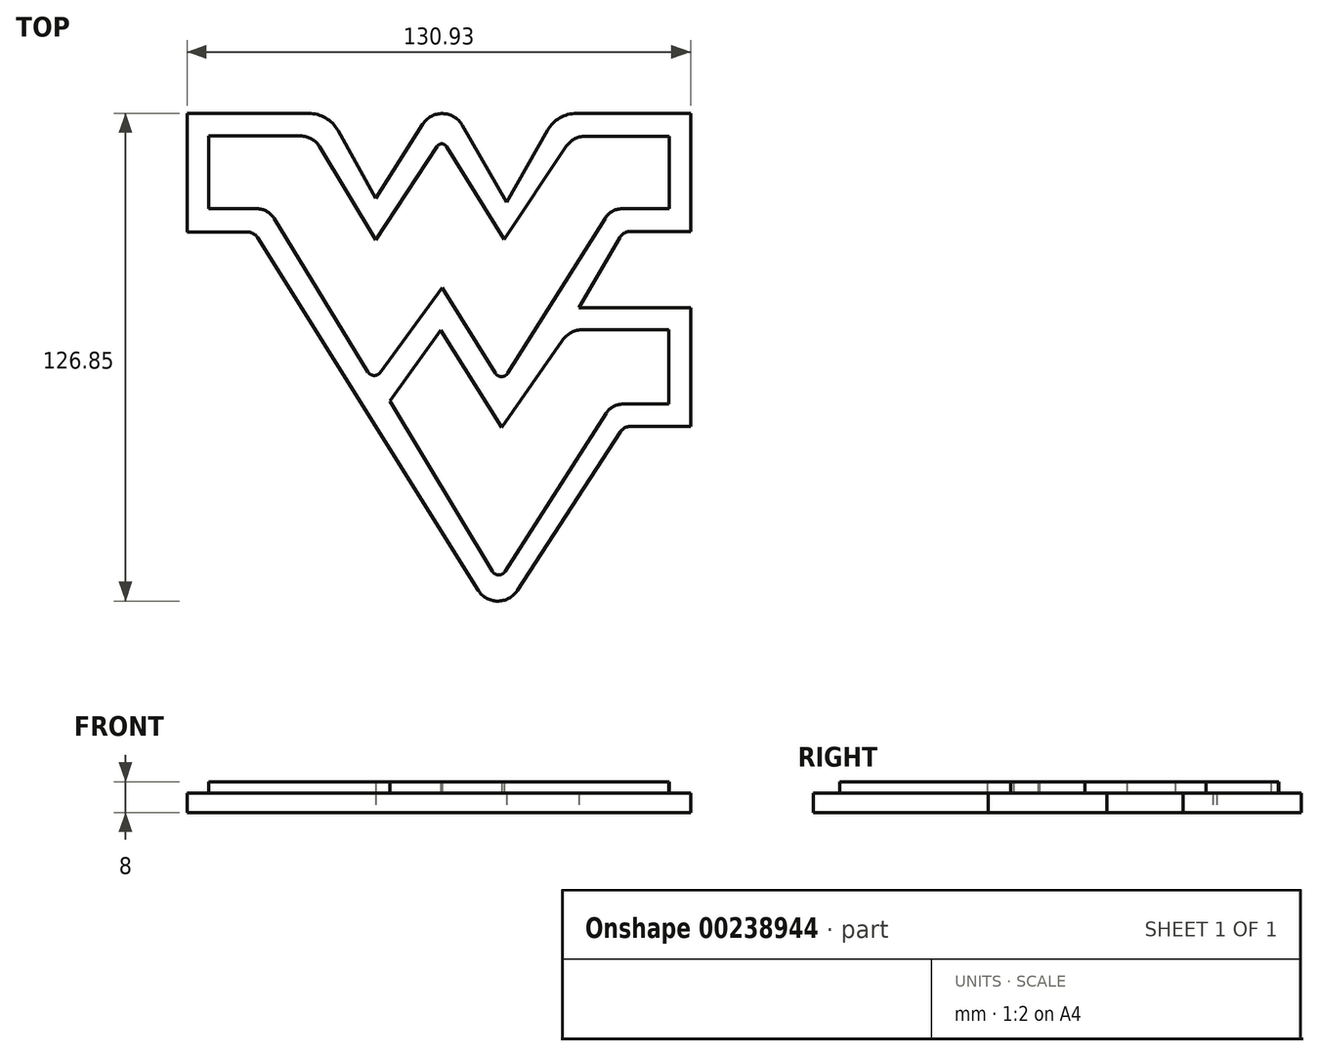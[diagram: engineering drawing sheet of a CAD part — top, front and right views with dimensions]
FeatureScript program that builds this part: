
annotation { "Feature Type Name" : "Feature", "Feature Type Description" : "" }
export const myFeature = defineFeature(function(context is Context, id is Id, definition is map)
    precondition{}
    {
        {
            var Q0;
            Q0=qCreatedBy(makeId("Top.planeOp"),FACE);
            var sketch = newSketch(context, id + "F0", { "sketchPlane" : qUnion([Q0])});
            skLineSegment(sketch, "E0", {"start": v(0, 0) * mm, "end": v(0, 127) * mm, "construction": true});
            skLineSegment(sketch, "E1", {"start": v(130.93, 127) * mm, "end": v(130.93, 96.28) * mm});
            skLineSegment(sketch, "E2", {"start": v(130.93, 45.55) * mm, "end": v(115.18, 45.55) * mm});
            skLineSegment(sketch, "E3", {"start": v(130.93, 76.4) * mm, "end": v(101.93, 76.4) * mm});
            skLineSegment(sketch, "E4", {"start": v(101.93, 76.4) * mm, "end": v(112.57, 94.78) * mm});
            skLineSegment(sketch, "E5", {"start": v(130.93, 96.28) * mm, "end": v(115.16, 96.28) * mm});
            skLineSegment(sketch, "E6", {"start": v(83.05, 103.92) * mm, "end": v(93.75, 122.62) * mm});
            skLineSegment(sketch, "E7", {"start": v(83.05, 103.92) * mm, "end": v(71.55, 123.94) * mm});
            skLineSegment(sketch, "E8", {"start": v(49.03, 104.93) * mm, "end": v(61.29, 124.17) * mm});
            skLineSegment(sketch, "E9", {"start": v(49.03, 104.93) * mm, "end": v(39.23, 122.53) * mm});
            skLineSegment(sketch, "E10", {"start": v(0, 96.14) * mm, "end": v(15.76, 96.14) * mm});
            skLineSegment(sketch, "E11", {"start": v(85.84, 2.88) * mm, "end": v(112.66, 44.18) * mm});
            skLineSegment(sketch, "E12", {"start": v(75.72, 2.96) * mm, "end": v(18.3, 94.73) * mm});
            skLineSegment(sketch, "E13.trimOffspring", {"start": v(63.09, 127) * mm, "end": v(69.8, 127) * mm});
            skLineSegment(sketch, "E14.trimOffspring", {"start": v(101.3, 127) * mm, "end": v(130.93, 127) * mm});
            skLineSegment(sketch, "E15", {"start": v(0, 127) * mm, "end": v(31.63, 127) * mm});
            skPoint(sketch, "E16.visualSharp", {"position": v(36.74, 127) * mm});
            skArc(sketch, "E16.filletArc", {"start": v(39.23, 122.53) * mm, "mid": v(36.04, 125.8) * mm, "end": v(31.63, 127) * mm});
            skPoint(sketch, "E17.visualSharp", {"position": v(96.25, 127) * mm});
            skArc(sketch, "E17.filletArc", {"start": v(101.3, 127) * mm, "mid": v(96.93, 125.83) * mm, "end": v(93.75, 122.62) * mm});
            skPoint(sketch, "E18.visualSharp", {"position": v(66.61, 132.54) * mm});
            skArc(sketch, "E18.filletArc", {"start": v(71.55, 123.94) * mm, "mid": v(66.49, 126.95) * mm, "end": v(61.29, 124.17) * mm});
            skLineSegment(sketch, "E19", {"start": v(80.71, -5.02) * mm, "end": v(0, -5.02) * mm, "construction": true});
            skLineSegment(sketch, "E20", {"start": v(0, -5.02) * mm, "end": v(0, 0) * mm, "construction": true});
            skPoint(sketch, "E21.visualSharp", {"position": v(80.71, -5.02) * mm});
            skArc(sketch, "E21.filletArc", {"start": v(75.72, 2.96) * mm, "mid": v(80.76, 0.15) * mm, "end": v(85.84, 2.88) * mm});
            skLineSegment(sketch, "E22.trimOffspring", {"start": v(130.93, 76.4) * mm, "end": v(130.93, 45.55) * mm});
            skPoint(sketch, "E23.visualSharp", {"position": v(17.42, 96.14) * mm});
            skArc(sketch, "E23.filletArc", {"start": v(18.3, 94.73) * mm, "mid": v(17.21, 95.76) * mm, "end": v(15.76, 96.14) * mm});
            skPoint(sketch, "E24.visualSharp", {"position": v(113.55, 45.55) * mm});
            skArc(sketch, "E24.filletArc", {"start": v(115.18, 45.55) * mm, "mid": v(113.75, 45.18) * mm, "end": v(112.66, 44.18) * mm});
            skPoint(sketch, "E25.visualSharp", {"position": v(113.43, 96.28) * mm});
            skArc(sketch, "E25.filletArc", {"start": v(115.16, 96.28) * mm, "mid": v(113.67, 95.88) * mm, "end": v(112.57, 94.78) * mm});
            skLineSegment(sketch, "E26", {"start": v(5.58, 121.12) * mm, "end": v(0, 121.12) * mm, "construction": true});
            skLineSegment(sketch, "E27", {"start": v(5.58, 121.12) * mm, "end": v(29.52, 121.12) * mm});
            skLineSegment(sketch, "E28", {"start": v(49.07, 94.16) * mm, "end": v(34.49, 118.31) * mm});
            skLineSegment(sketch, "E29", {"start": v(49.07, 94.16) * mm, "end": v(65.1, 118.45) * mm});
            skLineSegment(sketch, "E30", {"start": v(82.45, 94.25) * mm, "end": v(67.45, 118.42) * mm});
            skLineSegment(sketch, "E31", {"start": v(82.45, 94.25) * mm, "end": v(98.64, 118.46) * mm});
            skLineSegment(sketch, "E32", {"start": v(125.34, 121.03) * mm, "end": v(103.46, 121.03) * mm});
            skLineSegment(sketch, "E33", {"start": v(125.34, 102.18) * mm, "end": v(113.1, 102.18) * mm});
            skLineSegment(sketch, "E34", {"start": v(5.58, 121.12) * mm, "end": v(5.58, 102.18) * mm});
            skLineSegment(sketch, "E35", {"start": v(5.58, 102.18) * mm, "end": v(18.22, 102.18) * mm});
            skLineSegment(sketch, "E36", {"start": v(48.58, 57.31) * mm, "end": v(0, 57.31) * mm, "construction": true});
            skLineSegment(sketch, "E37", {"start": v(50.25, 59.61) * mm, "end": v(66.28, 81.66) * mm});
            skLineSegment(sketch, "E38", {"start": v(66.28, 81.66) * mm, "end": v(80.19, 59.43) * mm});
            skLineSegment(sketch, "E39", {"start": v(47.1, 59.74) * mm, "end": v(22.66, 99.7) * mm});
            skLineSegment(sketch, "E40", {"start": v(83.4, 59.43) * mm, "end": v(108.7, 99.74) * mm});
            skLineSegment(sketch, "E41", {"start": v(125.34, 102.18) * mm, "end": v(125.34, 121.03) * mm});
            skLineSegment(sketch, "E42", {"start": v(125.32, 51.4) * mm, "end": v(130.93, 51.4) * mm, "construction": true});
            skLineSegment(sketch, "E43", {"start": v(125.32, 51.4) * mm, "end": v(125.32, 70.76) * mm});
            skLineSegment(sketch, "E44", {"start": v(125.32, 70.76) * mm, "end": v(102.92, 70.76) * mm});
            skLineSegment(sketch, "E45", {"start": v(125.32, 51.4) * mm, "end": v(113.36, 51.4) * mm});
            skLineSegment(sketch, "E46", {"start": v(81.85, 45.3) * mm, "end": v(97.58, 67.96) * mm});
            skLineSegment(sketch, "E47", {"start": v(81.85, 45.3) * mm, "end": v(66, 70.66) * mm});
            skLineSegment(sketch, "E48", {"start": v(66, 70.66) * mm, "end": v(52.8, 52.2) * mm});
            skLineSegment(sketch, "E49", {"start": v(52.8, 52.2) * mm, "end": v(79.44, 7.88) * mm});
            skLineSegment(sketch, "E50", {"start": v(82.67, 7.83) * mm, "end": v(108.98, 49) * mm});
            skPoint(sketch, "E51.visualSharp", {"position": v(21.14, 102.18) * mm});
            skArc(sketch, "E51.filletArc", {"start": v(22.66, 99.7) * mm, "mid": v(20.77, 101.52) * mm, "end": v(18.22, 102.18) * mm});
            skPoint(sketch, "E52.visualSharp", {"position": v(110.23, 102.18) * mm});
            skArc(sketch, "E52.filletArc", {"start": v(113.1, 102.18) * mm, "mid": v(110.59, 101.53) * mm, "end": v(108.7, 99.74) * mm});
            skPoint(sketch, "E53.visualSharp", {"position": v(110.51, 51.4) * mm});
            skArc(sketch, "E53.filletArc", {"start": v(113.36, 51.4) * mm, "mid": v(110.86, 50.76) * mm, "end": v(108.98, 49) * mm});
            skPoint(sketch, "E54.visualSharp", {"position": v(48.58, 57.31) * mm});
            skArc(sketch, "E54.filletArc", {"start": v(47.1, 59.74) * mm, "mid": v(48.64, 58.83) * mm, "end": v(50.25, 59.61) * mm});
            skPoint(sketch, "E55.visualSharp", {"position": v(81.8, 56.86) * mm});
            skArc(sketch, "E55.filletArc", {"start": v(80.19, 59.43) * mm, "mid": v(81.8, 58.54) * mm, "end": v(83.4, 59.43) * mm});
            skPoint(sketch, "E56.visualSharp", {"position": v(81.02, 5.25) * mm});
            skArc(sketch, "E56.filletArc", {"start": v(79.44, 7.88) * mm, "mid": v(81.04, 6.95) * mm, "end": v(82.67, 7.83) * mm});
            skLineSegment(sketch, "E57", {"start": v(0, 127) * mm, "end": v(0, 96.14) * mm});
            skPoint(sketch, "E58.visualSharp", {"position": v(32.8, 121.12) * mm});
            skArc(sketch, "E58.filletArc", {"start": v(34.49, 118.31) * mm, "mid": v(32.37, 120.37) * mm, "end": v(29.52, 121.12) * mm});
            skPoint(sketch, "E59.visualSharp", {"position": v(100.37, 121.03) * mm});
            skArc(sketch, "E59.filletArc", {"start": v(103.46, 121.03) * mm, "mid": v(100.73, 120.35) * mm, "end": v(98.64, 118.46) * mm});
            skPoint(sketch, "E60.visualSharp", {"position": v(99.52, 70.76) * mm});
            skArc(sketch, "E60.filletArc", {"start": v(102.92, 70.76) * mm, "mid": v(99.9, 70.02) * mm, "end": v(97.58, 67.96) * mm});
            skPoint(sketch, "E61.visualSharp", {"position": v(66.3, 120.28) * mm});
            skArc(sketch, "E61.filletArc", {"start": v(67.45, 118.42) * mm, "mid": v(66.28, 119.08) * mm, "end": v(65.1, 118.45) * mm});
            skSolve(sketch);
        }
        {
            var Q0;
            Q0=makeQuery(id+"F0.imprint","IMPRINT",FACE,{"disambiguationData":[TD([[makeQuery(id+"F0.imprint","IMPRINT",EDGE,{"derivedFrom":sQuery(id+"F0.wireOp",EDGE,"E1")}),-1.0]])]});
            extrude(context, id + "F1", {"entities" : qUnion([Q0]), "depth" : 5 * mm});
        }
        {
            var Q0;
            Q0=makeQuery(id+"F0.imprint","IMPRINT",FACE,{"disambiguationData":[TD([[makeQuery(id+"F0.imprint","IMPRINT",EDGE,{"derivedFrom":sQuery(id+"F0.wireOp",EDGE,"E27")}),-1.0]])]});
            var Q1;
            Q1=makeQuery(id+"F0.imprint","IMPRINT",FACE,{"disambiguationData":[TD([[makeQuery(id+"F0.imprint","IMPRINT",EDGE,{"derivedFrom":sQuery(id+"F0.wireOp",EDGE,"E43")}),1.0]])]});
            extrude(context, id + "F2", {"entities" : qUnion([Q0, Q1]), "operationType" : NewBodyOperationType.ADD, "depth" : 8 * mm});
        }
    });
